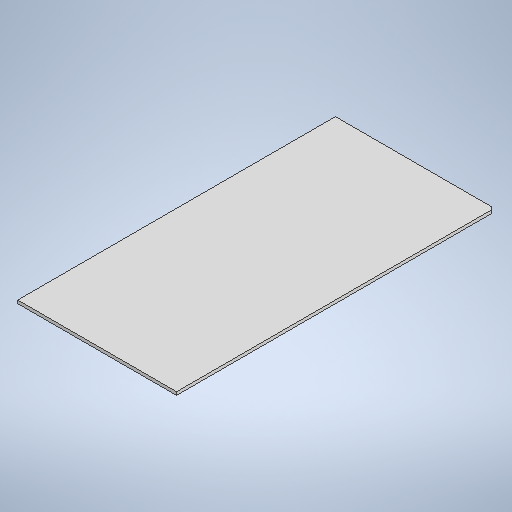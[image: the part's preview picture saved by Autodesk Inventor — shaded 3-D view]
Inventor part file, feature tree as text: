
AUTODESK INVENTOR PART (.ipt)
format: ipt  version: 2025 (Build 290162010, 162A)  size: 330,240 bytes
history: native  units: mm
features: other x4, sketch x2, sheet_metal_op x1, chamfer x1
ambient origin geometry x8: Origin, YZ Plane, XZ Plane, XY Plane, X Axis, Y Axis, Z Axis, Center Point
bodies: Solid1 (feature_tree)
feature tree (8):
  sheet_metal_op  "Face1"
  chamfer  "Chamfer1"  Distance=2.0mm
  other  "Mark1"
  other  "A-Side Definition"
  sketch  "Sketch1"  dims[d0=100.0mm]
  other  "Plate1"
  sketch  "Sketch2"  dims[d1=200.0mm d2=2.0mm d3=2.0mm d4=2.0mm d5=45.0deg d6=200.0mm d9=20.0mm d10=20.0mm d11=20.0mm]
  other  "Definition1"
